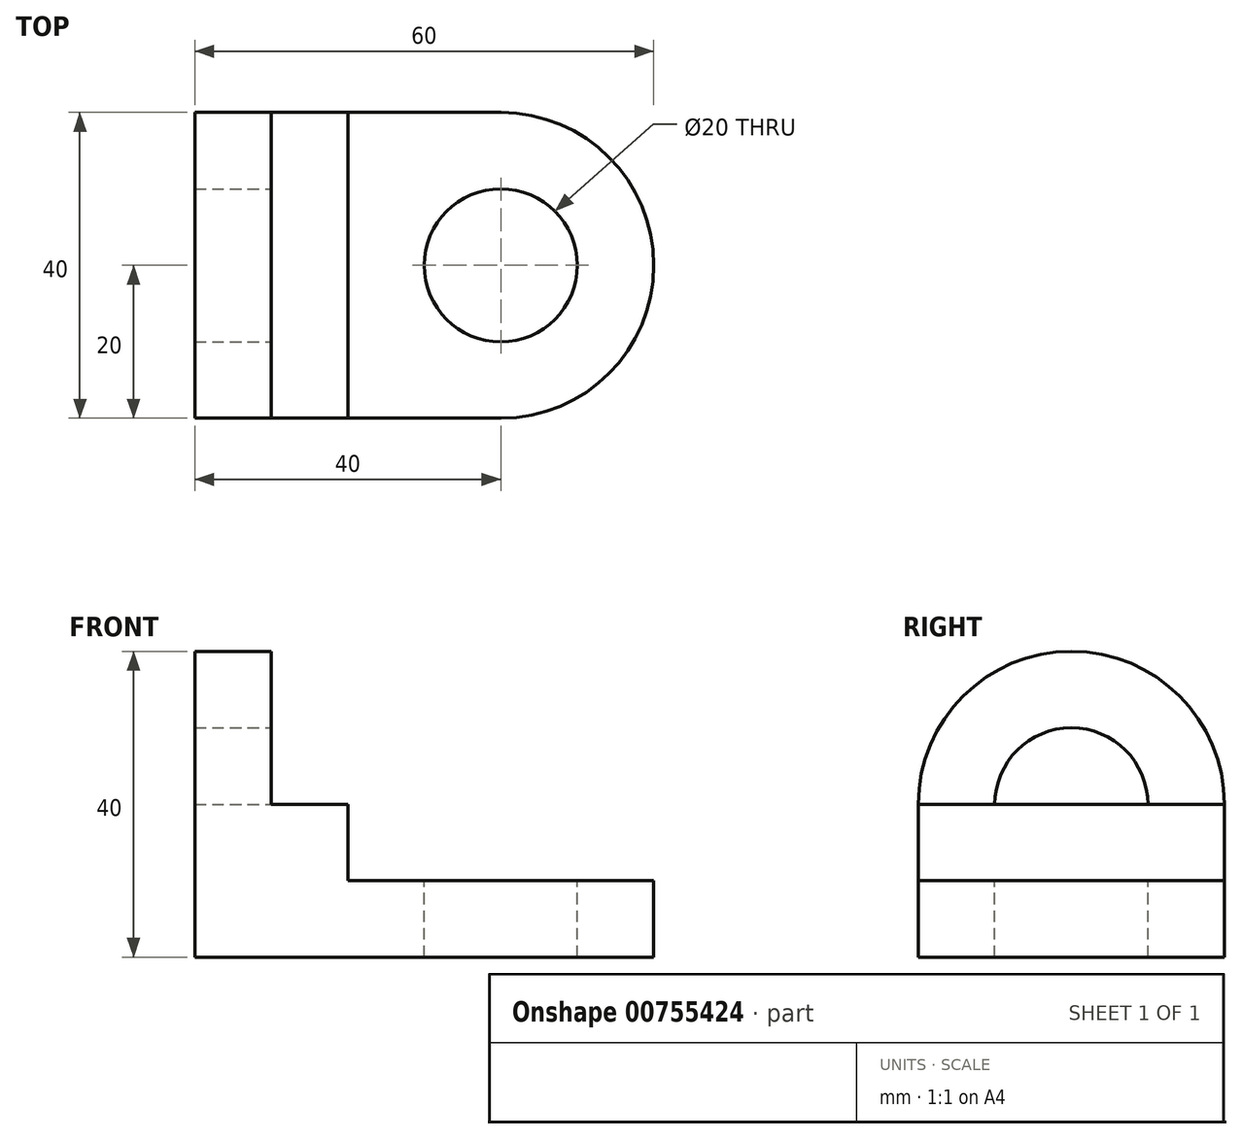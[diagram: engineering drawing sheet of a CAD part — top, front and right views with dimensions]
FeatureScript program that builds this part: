
annotation { "Feature Type Name" : "Feature", "Feature Type Description" : "" }
export const myFeature = defineFeature(function(context is Context, id is Id, definition is map)
    precondition{}
    {
        {
            var Q0;
            Q0=qCreatedBy(makeId("Top.planeOp"),FACE);
            var sketch = newSketch(context, id + "F0", { "sketchPlane" : qUnion([Q0])});
            skLineSegment(sketch, "E0", {"start": v(0, 0) * mm, "end": v(0, 40) * mm});
            skLineSegment(sketch, "E1", {"start": v(0, 40) * mm, "end": v(60, 40) * mm});
            skLineSegment(sketch, "E2", {"start": v(60, 40) * mm, "end": v(60, 0) * mm});
            skLineSegment(sketch, "E3", {"start": v(60, 0) * mm, "end": v(0, 0) * mm});
            skSolve(sketch);
        }
        {
            var Q0;
            Q0=makeQuery(id+"F0.imprint","IMPRINT",FACE,{"disambiguationData":[TD([[makeQuery(id+"F0.imprint","IMPRINT",EDGE,{"derivedFrom":sQuery(id+"F0.wireOp",EDGE,"E0")}),-1.0]])]});
            extrude(context, id + "F1", {"entities" : qUnion([Q0]), "depth" : 40 * mm, "offsetDistance" : 25 * mm});
        }
        {
            var Q0;
            Q0=makeQuery(id+"F1.opExtrude","CAP_FACE",FACE,{"disambiguationData":[OSD([sQuery(id+"F0.wireOp",EDGE,"E0"),sQuery(id+"F0.wireOp",EDGE,"E1"),sQuery(id+"F0.wireOp",EDGE,"E2"),sQuery(id+"F0.wireOp",EDGE,"E3")])],"isStart":false});
            var sketch = newSketch(context, id + "F2", { "sketchPlane" : qUnion([Q0])});
            skLineSegment(sketch, "E4.bottom", {"start": v(0, 40) * mm, "end": v(10, 40) * mm});
            skLineSegment(sketch, "E4.top", {"start": v(0, 0) * mm, "end": v(10, 0) * mm});
            skLineSegment(sketch, "E4.left", {"start": v(0, 40) * mm, "end": v(0, 0) * mm});
            skLineSegment(sketch, "E4.right", {"start": v(10, 40) * mm, "end": v(10, 0) * mm});
            skSolve(sketch);
        }
        {
            var Q0;
            {var subQ0=sQuery(id+"F2.wireOp",EDGE,"E4.right");Q0=makeQuery(id+"F2.imprint","IMPRINT",FACE,{"disambiguationData":[TD([[makeQuery(id+"F2.imprint","IMPRINT",EDGE,{"derivedFrom":subQ0}),1.0]])]});}
            extrude(context, id + "F3", {"entities" : qUnion([Q0]), "operationType" : NewBodyOperationType.REMOVE, "oppositeDirection" : true, "depth" : 30 * mm, "offsetDistance" : 25 * mm});
        }
        {
            var Q0;
            Q0=makeQuery(id+"F3.boolean.opBoolean","COPY",FACE,{"derivedFrom":makeQuery(id+"F3.opExtrude","CAP_FACE",FACE,{"disambiguationData":[OSD([sQuery(id+"F0.wireOp",EDGE,"E1"),sQuery(id+"F0.wireOp",EDGE,"E2"),sQuery(id+"F0.wireOp",EDGE,"E3"),sQuery(id+"F2.wireOp",EDGE,"E4.right")])],"isStart":false})});
            var sketch = newSketch(context, id + "F4", { "sketchPlane" : qUnion([Q0])});
            skLineSegment(sketch, "E5.bottom", {"start": v(10, 40) * mm, "end": v(20, 40) * mm});
            skLineSegment(sketch, "E5.top", {"start": v(10, 0) * mm, "end": v(20, 0) * mm});
            skLineSegment(sketch, "E5.left", {"start": v(10, 40) * mm, "end": v(10, 0) * mm});
            skLineSegment(sketch, "E5.right", {"start": v(20, 40) * mm, "end": v(20, 0) * mm});
            skSolve(sketch);
        }
        {
            var Q0;
            Q0=makeQuery(id+"F4.imprint","IMPRINT",FACE,{"disambiguationData":[TD([[makeQuery(id+"F4.imprint","IMPRINT",EDGE,{"derivedFrom":sQuery(id+"F4.wireOp",EDGE,"E5.bottom")}),-1.0]])]});
            extrude(context, id + "F5", {"entities" : qUnion([Q0]), "operationType" : NewBodyOperationType.ADD, "depth" : 10 * mm, "offsetDistance" : 25 * mm});
        }
        {
            var Q0;
            Q0=makeQuery(id+"F1.opExtrude","CAP_EDGE",EDGE,{"disambiguationData":[OSD([sQuery(id+"F0.wireOp",EDGE,"E3")])],"isStart":false});
            var Q1;
            Q1=makeQuery(id+"F1.opExtrude","CAP_EDGE",EDGE,{"disambiguationData":[OSD([sQuery(id+"F0.wireOp",EDGE,"E1")])],"isStart":false});
            fillet(context, id + "F6", {"entities" : qUnion([Q0, Q1]), "radius" : 20 * mm, "tangentPropagation" : true, "allowEdgeOverflow" : false});
        }
        {
            var Q0;
            Q0=makeQuery(id+"F1.opExtrude","SWEPT_EDGE",EDGE,{"disambiguationData":[OSD([sQuery(id+"F0.wireOp",EDGE,"E1"),sQuery(id+"F0.wireOp",EDGE,"E2")])]});
            var Q1;
            Q1=makeQuery(id+"F1.opExtrude","SWEPT_EDGE",EDGE,{"disambiguationData":[OSD([sQuery(id+"F0.wireOp",EDGE,"E2"),sQuery(id+"F0.wireOp",EDGE,"E3")])]});
            fillet(context, id + "F7", {"entities" : qUnion([Q0, Q1]), "radius" : 20 * mm, "tangentPropagation" : true, "allowEdgeOverflow" : false});
        }
        {
            var Q0;
            Q0=makeQuery(id+"F3.boolean.opBoolean","COPY",FACE,{"derivedFrom":makeQuery(id+"F3.opExtrude","SWEPT_FACE",FACE,{"disambiguationData":[OSD([sQuery(id+"F2.wireOp",EDGE,"E4.right")])]})});
            var sketch = newSketch(context, id + "F8", { "sketchPlane" : qUnion([Q0])});
            skCircle(sketch, "E6", {"center": v(20, 20) * mm, "radius": 10 * mm});
            skSolve(sketch);
        }
        {
            var Q0;
            {var subQ0=sQuery(id+"F8.wireOp",EDGE,"E6");var subQ1=makeQuery(id+"F5.opExtrude","CAP_EDGE",EDGE,{"disambiguationData":[OSD([sQuery(id+"F4.wireOp",EDGE,"E5.left")])],"isStart":false});var subQ2=makeQuery(id+"F8.imprint","INTERSECT",VERTEX,{"disambiguationData":[OD(0.0)],"derivedFrom":[subQ1,subQ0]});Q0=makeQuery(id+"F8.imprint","IMPRINT",FACE,{"disambiguationData":[TD([[makeQuery(id+"F8.imprint","IMPRINT",EDGE,{"disambiguationData":[TD([[subQ2,-1.0]])],"derivedFrom":subQ0}),1.0]])]});}
            extrude(context, id + "F9", {"entities" : qUnion([Q0]), "operationType" : NewBodyOperationType.REMOVE, "oppositeDirection" : true, "depth" : 25 * mm, "offsetDistance" : 25 * mm});
        }
        {
            var Q0;
            Q0=makeQuery(id+"F5.opExtrude","SWEPT_FACE",FACE,{"disambiguationData":[OSD([sQuery(id+"F4.wireOp",EDGE,"E5.right")])]});
            var sketch = newSketch(context, id + "F10", { "sketchPlane" : qUnion([Q0])});
            skCircle(sketch, "E7", {"center": v(20, 20) * mm, "radius": 10 * mm});
            skSolve(sketch);
        }
        {
            var Q0;
            {var subQ0=sQuery(id+"F10.wireOp",EDGE,"E7");var subQ1=sQuery(id+"F4.wireOp",EDGE,"E5.right");var subQ2=makeQuery(id+"F5.opExtrude","CAP_EDGE",EDGE,{"disambiguationData":[OSD([subQ1])],"isStart":false});var subQ3=makeQuery(id+"F10.imprint","INTERSECT",VERTEX,{"disambiguationData":[OD(0.0)],"derivedFrom":[subQ2,subQ0]});Q0=makeQuery(id+"F10.imprint","IMPRINT",FACE,{"disambiguationData":[TD([[makeQuery(id+"F10.imprint","IMPRINT",EDGE,{"disambiguationData":[TD([[subQ3,-1.0]])],"derivedFrom":subQ0}),1.0]])]});}
            extrude(context, id + "F11", {"entities" : qUnion([Q0]), "operationType" : NewBodyOperationType.REMOVE, "oppositeDirection" : true, "depth" : 25 * mm, "offsetDistance" : 25 * mm});
        }
        {
            var Q0;
            Q0=makeQuery(id+"F3.boolean.opBoolean","COPY",FACE,{"derivedFrom":makeQuery(id+"F3.opExtrude","CAP_FACE",FACE,{"disambiguationData":[OSD([sQuery(id+"F0.wireOp",EDGE,"E1"),sQuery(id+"F0.wireOp",EDGE,"E2"),sQuery(id+"F0.wireOp",EDGE,"E3"),sQuery(id+"F2.wireOp",EDGE,"E4.right")])],"isStart":false})});
            var sketch = newSketch(context, id + "F12", { "sketchPlane" : qUnion([Q0])});
            skCircle(sketch, "E8", {"center": v(40, 20) * mm, "radius": 10 * mm});
            skSolve(sketch);
        }
        {
            var Q0;
            Q0=makeQuery(id+"F12.imprint","IMPRINT",FACE,{"disambiguationData":[TD([[makeQuery(id+"F12.imprint","IMPRINT",EDGE,{"derivedFrom":sQuery(id+"F12.wireOp",EDGE,"E8")}),1.0]])]});
            extrude(context, id + "F13", {"entities" : qUnion([Q0]), "operationType" : NewBodyOperationType.REMOVE, "oppositeDirection" : true, "depth" : 25 * mm, "offsetDistance" : 25 * mm});
        }
    });
